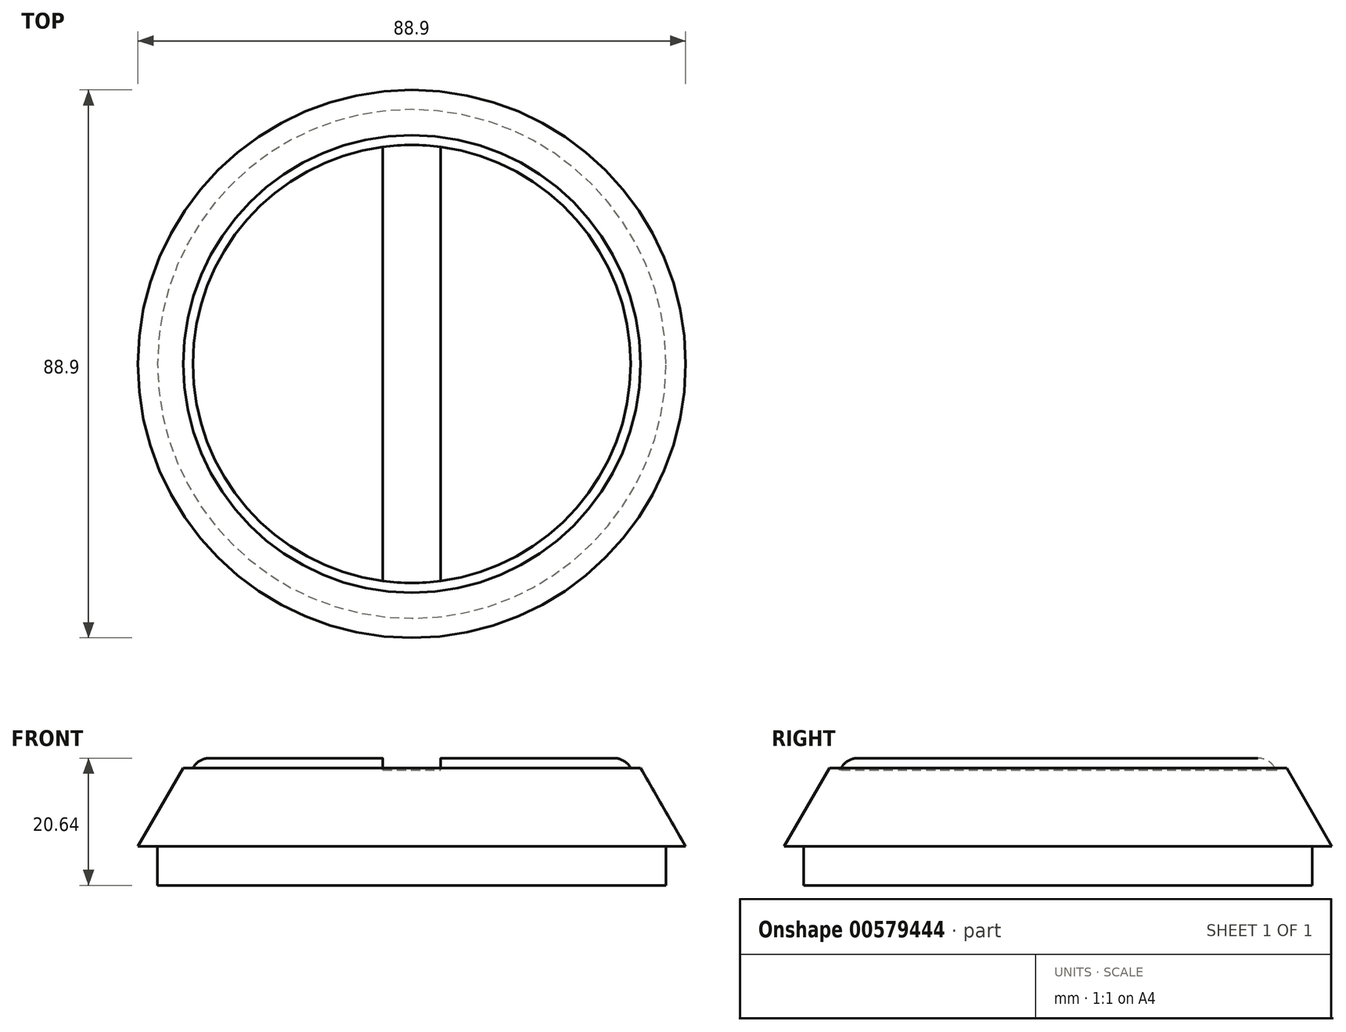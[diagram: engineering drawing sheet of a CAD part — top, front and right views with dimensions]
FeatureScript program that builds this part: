
annotation { "Feature Type Name" : "Feature", "Feature Type Description" : "" }
export const myFeature = defineFeature(function(context is Context, id is Id, definition is map)
    precondition{}
    {
        {
            var Q0;
            Q0=qCreatedBy(makeId("Top.planeOp"),FACE);
            var sketch = newSketch(context, id + "F0", { "sketchPlane" : qUnion([Q0])});
            skCircle(sketch, "E0", {"center": v(0, 0) * mm, "radius": 44.45 * mm});
            skCircle(sketch, "E1", {"center": v(0, 0) * mm, "radius": 41.28 * mm});
            skSolve(sketch);
        }
        {
            var Q0;
            Q0=makeQuery(id+"F0.imprint","IMPRINT",FACE,{"disambiguationData":[TD([[makeQuery(id+"F0.imprint","IMPRINT",EDGE,{"derivedFrom":sQuery(id+"F0.wireOp",EDGE,"E1")}),1.0]])]});
            var Q1;
            Q1=makeQuery(id+"F0.imprint","IMPRINT",FACE,{"disambiguationData":[TD([[makeQuery(id+"F0.imprint","IMPRINT",EDGE,{"derivedFrom":sQuery(id+"F0.wireOp",EDGE,"E0")}),1.0]])]});
            extrude(context, id + "F1", {"entities" : qUnion([Q0, Q1]), "depth" : 12.7 * mm, "offsetDistance" : 25.4 * mm, "hasDraft" : true, "draftAngle" : 30 * degree, "draftPullDirection" : true});
        }
        {
            var Q0;
            Q0=makeQuery(id+"F0.imprint","IMPRINT",FACE,{"disambiguationData":[TD([[makeQuery(id+"F0.imprint","IMPRINT",EDGE,{"derivedFrom":sQuery(id+"F0.wireOp",EDGE,"E1")}),1.0]])]});
            extrude(context, id + "F2", {"entities" : qUnion([Q0]), "operationType" : NewBodyOperationType.ADD, "oppositeDirection" : true, "depth" : 6.35 * mm, "offsetDistance" : 25.4 * mm});
        }
        {
            var Q0;
            Q0=makeQuery(id+"F1.opExtrude","CAP_FACE",FACE,{"disambiguationData":[OSD([sQuery(id+"F0.wireOp",EDGE,"E0")])],"isStart":false});
            var sketch = newSketch(context, id + "F3", { "sketchPlane" : qUnion([Q0])});
            skCircle(sketch, "E2.0", {"center": v(0, 0) * mm, "radius": 35.53 * mm});
            skSolve(sketch);
        }
        {
            var Q0;
            Q0=makeQuery(id+"F3.imprint","IMPRINT",FACE,{"disambiguationData":[TD([[makeQuery(id+"F3.imprint","IMPRINT",EDGE,{"derivedFrom":sQuery(id+"F3.wireOp",EDGE,"E2.0")}),1.0]])]});
            extrude(context, id + "F4", {"entities" : qUnion([Q0]), "operationType" : NewBodyOperationType.ADD, "depth" : 1.59 * mm, "offsetDistance" : 25.4 * mm});
        }
        {
            var Q0;
            Q0=makeQuery(id+"F4.opExtrude","CAP_EDGE",EDGE,{"disambiguationData":[OSD([sQuery(id+"F3.wireOp",EDGE,"E2.0")])],"isStart":false});
            fillet(context, id + "F5", {"entities" : qUnion([Q0]), "radius" : 3.17 * mm, "tangentPropagation" : true, "allowEdgeOverflow" : false});
        }
        {
            var Q0;
            Q0=makeQuery(id+"F1.opExtrude","CAP_FACE",FACE,{"disambiguationData":[OSD([sQuery(id+"F0.wireOp",EDGE,"E0")])],"isStart":false});
            var sketch = newSketch(context, id + "F6", { "sketchPlane" : qUnion([Q0])});
            skLineSegment(sketch, "E3.bottom", {"start": v(4.71, -40.13) * mm, "end": v(-4.71, -40.13) * mm});
            skLineSegment(sketch, "E3.top", {"start": v(4.71, 40.13) * mm, "end": v(-4.71, 40.13) * mm});
            skLineSegment(sketch, "E3.left", {"start": v(4.71, -40.13) * mm, "end": v(4.71, 40.13) * mm});
            skLineSegment(sketch, "E3.right", {"start": v(-4.71, -40.13) * mm, "end": v(-4.71, 40.13) * mm});
            skPoint(sketch, "E3.middle", {"position": v(0, 0) * mm});
            skCircle(sketch, "E4", {"center": v(0, 0) * mm, "radius": 35.32 * mm});
            skSolve(sketch);
        }
        {
            var Q0;
            {var subQ0=sQuery(id+"F6.wireOp",EDGE,"E4");var subQ1=sQuery(id+"F6.wireOp",EDGE,"E3.left");var subQ2=makeQuery(id+"F6.imprint","INTERSECT",VERTEX,{"disambiguationData":[OD(0.0)],"derivedFrom":[subQ1,subQ0]});Q0=makeQuery(id+"F6.imprint","IMPRINT",FACE,{"disambiguationData":[TD([[makeQuery(id+"F6.imprint","IMPRINT",EDGE,{"disambiguationData":[TD([[subQ2,-1.0]])],"derivedFrom":subQ1}),1.0]])]});}
            var Q1;
            {var subQ0=sQuery(id+"F6.wireOp",EDGE,"E4");var subQ1=sQuery(id+"F6.wireOp",EDGE,"E3.left");var subQ2=makeQuery(id+"F6.imprint","INTERSECT",VERTEX,{"disambiguationData":[OD(0.0)],"derivedFrom":[subQ1,subQ0]});Q1=makeQuery(id+"F6.imprint","IMPRINT",FACE,{"disambiguationData":[TD([[makeQuery(id+"F6.imprint","IMPRINT",EDGE,{"disambiguationData":[TD([[subQ2,1.0]])],"derivedFrom":subQ0}),-1.0]])]});}
            var Q2;
            {var subQ0=sQuery(id+"F6.wireOp",EDGE,"E4");var subQ1=sQuery(id+"F6.wireOp",EDGE,"E3.left");var subQ2=makeQuery(id+"F6.imprint","INTERSECT",VERTEX,{"disambiguationData":[OD(1.0)],"derivedFrom":[subQ1,subQ0]});Q2=makeQuery(id+"F6.imprint","IMPRINT",FACE,{"disambiguationData":[TD([[makeQuery(id+"F6.imprint","IMPRINT",EDGE,{"disambiguationData":[TD([[subQ2,-1.0]])],"derivedFrom":subQ0}),-1.0]])]});}
            extrude(context, id + "F7", {"entities" : qUnion([Q0, Q1, Q2]), "operationType" : NewBodyOperationType.REMOVE, "depth" : 2.95 * mm, "offsetDistance" : 25.4 * mm});
        }
        {
            var Q0;
            {var subQ0=sQuery(id+"F6.wireOp",EDGE,"E4");var subQ1=sQuery(id+"F6.wireOp",EDGE,"E3.left");var subQ2=makeQuery(id+"F6.imprint","INTERSECT",VERTEX,{"disambiguationData":[OD(0.0)],"derivedFrom":[subQ1,subQ0]});Q0=makeQuery(id+"F6.imprint","IMPRINT",FACE,{"disambiguationData":[TD([[makeQuery(id+"F6.imprint","IMPRINT",EDGE,{"disambiguationData":[TD([[subQ2,1.0]])],"derivedFrom":subQ0}),-1.0]])]});}
            var Q1;
            {var subQ0=sQuery(id+"F6.wireOp",EDGE,"E4");var subQ1=sQuery(id+"F6.wireOp",EDGE,"E3.left");var subQ2=makeQuery(id+"F6.imprint","INTERSECT",VERTEX,{"disambiguationData":[OD(0.0)],"derivedFrom":[subQ1,subQ0]});Q1=makeQuery(id+"F6.imprint","IMPRINT",FACE,{"disambiguationData":[TD([[makeQuery(id+"F6.imprint","IMPRINT",EDGE,{"disambiguationData":[TD([[subQ2,-1.0]])],"derivedFrom":subQ1}),1.0]])]});}
            var Q2;
            {var subQ0=sQuery(id+"F6.wireOp",EDGE,"E4");var subQ1=sQuery(id+"F6.wireOp",EDGE,"E3.left");var subQ2=makeQuery(id+"F6.imprint","INTERSECT",VERTEX,{"disambiguationData":[OD(1.0)],"derivedFrom":[subQ1,subQ0]});Q2=makeQuery(id+"F6.imprint","IMPRINT",FACE,{"disambiguationData":[TD([[makeQuery(id+"F6.imprint","IMPRINT",EDGE,{"disambiguationData":[TD([[subQ2,-1.0]])],"derivedFrom":subQ0}),-1.0]])]});}
            extrude(context, id + "F8", {"entities" : qUnion([Q0, Q1, Q2]), "operationType" : NewBodyOperationType.REMOVE, "oppositeDirection" : true, "depth" : 0.32 * mm, "offsetDistance" : 25.4 * mm});
        }
    });
